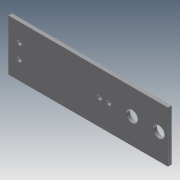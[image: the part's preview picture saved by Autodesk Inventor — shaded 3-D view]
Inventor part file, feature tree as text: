
AUTODESK INVENTOR PART (.ipt)
format: ipt  version: 2011 (Build 150239000, 239)  size: 124,416 bytes
history: native  units: in
note: dims shown in document units (in); Inventor stores cm internally (conversion verified against a paired STEP export)
features: extrude x7, sketch x7
ambient origin geometry x8: Origin, YZ Plane, XZ Plane, XY Plane, X Axis, Y Axis, Z Axis, Center Point
bodies: Solid1 (feature_tree)
feature tree (14):
  extrude  "Extrusion1"  Depth=1.26in
  extrude  "Extrusion2"  Depth=0.5in TaperAngle=0.0deg
  extrude  "Extrusion3"  Depth=0.25in
  extrude  "Extrusion4"  Depth=0.156in
  extrude  "Extrusion5"  Depth=0.315in
  extrude  "Extrusion6"  Depth=0.5in TaperAngle=0.0deg
  extrude  "Extrusion7"  Depth=0.315in
  sketch  "Sketch1"  dims[d0=5.5in d1=1.26in]
  sketch  "Sketch2"  dims[d2=0.125in d3=0.0in d4=0.5in d5=0.0in]
  sketch  "Sketch3"  dims[d6=0.75in d7=0.25in]
  sketch  "Sketch4"  dims[d8=0.25in d9=0.156in]
  sketch  "Sketch5"  dims[d10=0.5in d11=0.0in d12=0.315in]
  sketch  "Sketch6"  dims[d13=0.394in d14=0.5in d15=0.0in]
  sketch  "Sketch7"  dims[d16=0.125in d17=0.0in d18=0.315in d19=0.3937in d20=1.1811in d21=0.125in d22=0.0in d23=0.75in d24=2.71in d25=0.32in d26=0.156in d27=0.156in d28=1.0in d29=0.0in]
